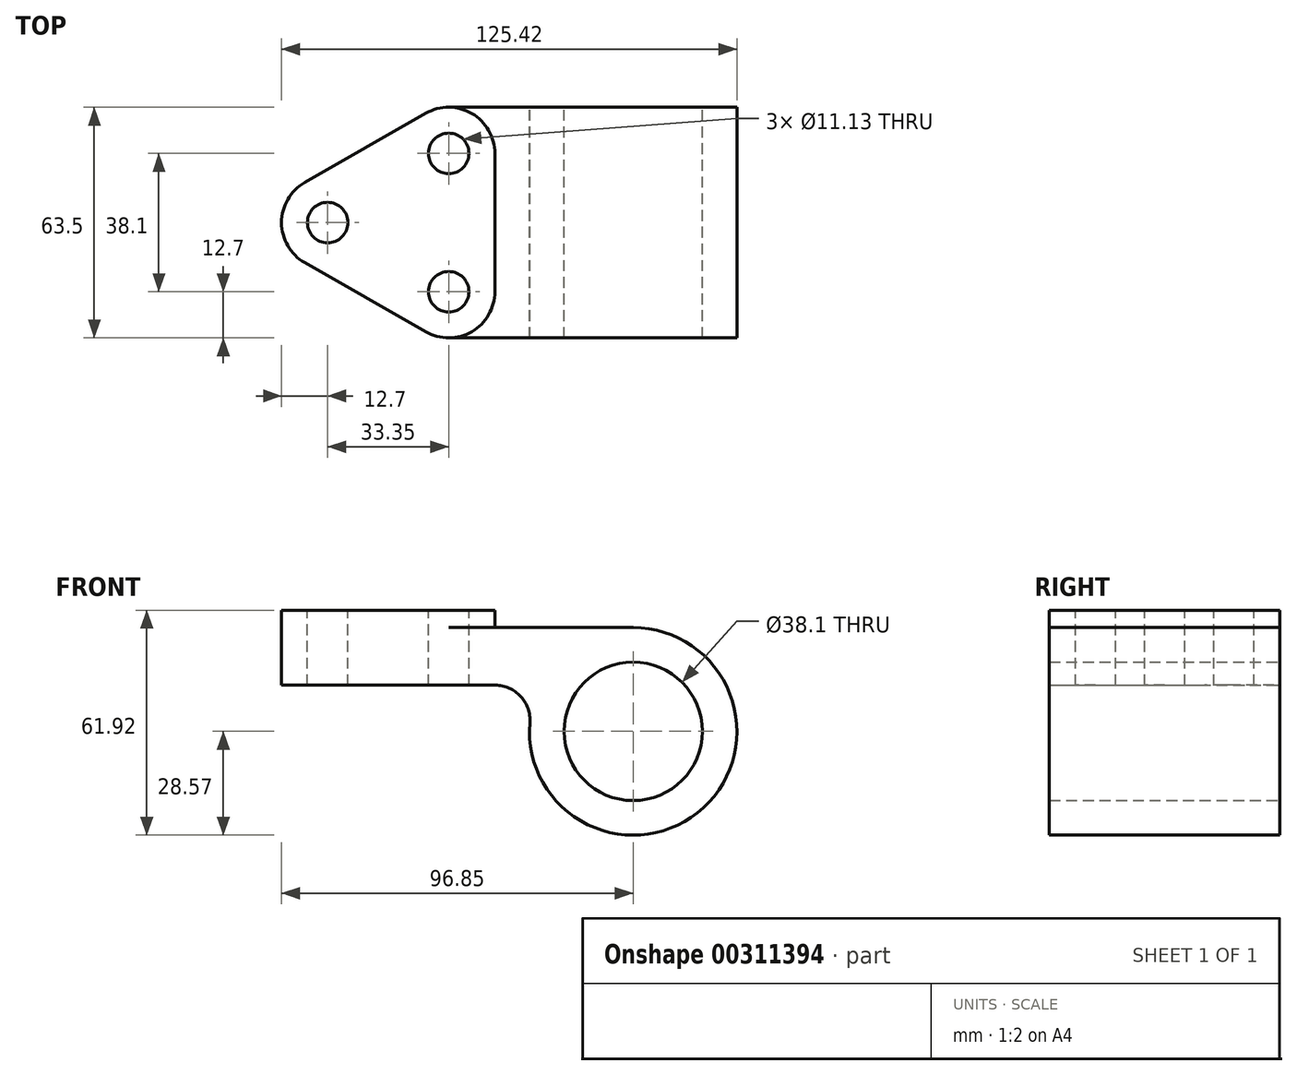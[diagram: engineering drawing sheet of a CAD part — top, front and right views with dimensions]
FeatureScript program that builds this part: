
annotation { "Feature Type Name" : "Feature", "Feature Type Description" : "" }
export const myFeature = defineFeature(function(context is Context, id is Id, definition is map)
    precondition{}
    {
        {
            var Q0;
            Q0=qCreatedBy(makeId("Front.planeOp"),FACE);
            var sketch = newSketch(context, id + "F0", { "sketchPlane" : qUnion([Q0])});
            skArc(sketch, "E0", {"start": v(-28.48, 2.38) * mm, "mid": v(19.35, -21.03) * mm, "end": v(0, 28.58) * mm});
            skCircle(sketch, "E1", {"center": v(0, 0) * mm, "radius": 19.05 * mm});
            skLineSegment(sketch, "E2", {"start": v(-37.97, 12.7) * mm, "end": v(-96.85, 12.7) * mm});
            skLineSegment(sketch, "E3", {"start": v(-96.85, 12.7) * mm, "end": v(-96.85, 28.57) * mm});
            skLineSegment(sketch, "E4", {"start": v(-38.1, 28.57) * mm, "end": v(0, 28.57) * mm});
            skLineSegment(sketch, "E5", {"start": v(-38.1, 28.57) * mm, "end": v(-38.1, 33.35) * mm});
            skLineSegment(sketch, "E6", {"start": v(-38.1, 33.35) * mm, "end": v(-96.85, 33.35) * mm});
            skLineSegment(sketch, "E7", {"start": v(-96.85, 33.35) * mm, "end": v(-96.85, 28.57) * mm});
            skPoint(sketch, "E8.visualSharp", {"position": v(-25.6, 12.7) * mm});
            skArc(sketch, "E8.filletArc", {"start": v(-28.48, 2.38) * mm, "mid": v(-30.96, 9.62) * mm, "end": v(-37.97, 12.7) * mm});
            skSolve(sketch);
        }
        {
            var Q0;
            Q0 = qSketchRegion(id + "F0", true);
            extrude(context, id + "F1", {"entities" : qUnion([Q0]), "depth" : 63.5 * mm});
        }
        {
            var Q0;
            Q0=makeQuery(id+"F1.opExtrude","SWEPT_FACE",FACE,{"disambiguationData":[OSD([sQuery(id+"F0.wireOp",EDGE,"E6")])]});
            var sketch = newSketch(context, id + "F2", { "sketchPlane" : qUnion([Q0])});
            skArc(sketch, "E9", {"start": v(-90.45, -20.72) * mm, "mid": v(-96.85, -31.75) * mm, "end": v(-90.45, -42.78) * mm});
            skPoint(sketch, "E9.centerSnap0", {"position": v(-38.1, -31.75) * mm});
            skArc(sketch, "E10", {"start": v(-38.1, -12.7) * mm, "mid": v(-44.42, -1.72) * mm, "end": v(-57.1, -1.67) * mm});
            skArc(sketch, "E11", {"start": v(-57.1, -61.83) * mm, "mid": v(-44.42, -61.78) * mm, "end": v(-38.1, -50.8) * mm});
            skLineSegment(sketch, "E12", {"start": v(-90.45, -20.72) * mm, "end": v(-57.1, -1.67) * mm});
            skLineSegment(sketch, "E13", {"start": v(-90.45, -42.78) * mm, "end": v(-57.1, -61.83) * mm});
            skLineSegment(sketch, "E14", {"start": v(-38.1, -12.7) * mm, "end": v(-38.1, -50.8) * mm});
            skCircle(sketch, "E15", {"center": v(-84.15, -31.75) * mm, "radius": 5.56 * mm});
            skCircle(sketch, "E16", {"center": v(-50.8, -12.7) * mm, "radius": 5.56 * mm});
            skCircle(sketch, "E17", {"center": v(-50.8, -50.8) * mm, "radius": 5.56 * mm});
            skSolve(sketch);
        }
        {
            var Q0;
            {var subQ6=sQuery(id+"F2.wireOp",EDGE,"E12");Q0=makeQuery(id+"F2.imprint","IMPRINT",FACE,{"disambiguationData":[TD([[makeQuery(id+"F2.imprint","IMPRINT",EDGE,{"derivedFrom":subQ6}),1.0]])]});}
            var Q1;
            {var subQ6=sQuery(id+"F2.wireOp",EDGE,"E13");Q1=makeQuery(id+"F2.imprint","IMPRINT",FACE,{"disambiguationData":[TD([[makeQuery(id+"F2.imprint","IMPRINT",EDGE,{"derivedFrom":subQ6}),-1.0]])]});}
            var Q2;
            {var subQ0=sQuery(id+"F2.wireOp",EDGE,"E11");var subQ1=sQuery(id+"F0.wireOp",EDGE,"E6");var subQ4=makeQuery(id+"F1.opExtrude","CAP_EDGE",EDGE,{"disambiguationData":[OSD([subQ1])],"isStart":false});var subQ5=makeQuery(id+"F2.imprint","INTERSECT",VERTEX,{"derivedFrom":[subQ4,subQ0]});Q2=makeQuery(id+"F2.imprint","IMPRINT",FACE,{"disambiguationData":[TD([[makeQuery(id+"F2.imprint","IMPRINT",EDGE,{"disambiguationData":[TD([[subQ5,1.0]])],"derivedFrom":subQ4}),-1.0]])]});}
            var Q3;
            {var subQ0=sQuery(id+"F2.wireOp",EDGE,"E10");var subQ1=sQuery(id+"F0.wireOp",EDGE,"E6");var subQ4=makeQuery(id+"F1.opExtrude","CAP_EDGE",EDGE,{"disambiguationData":[OSD([subQ1])],"isStart":true});var subQ5=makeQuery(id+"F2.imprint","INTERSECT",VERTEX,{"derivedFrom":[subQ4,subQ0]});Q3=makeQuery(id+"F2.imprint","IMPRINT",FACE,{"disambiguationData":[TD([[makeQuery(id+"F2.imprint","IMPRINT",EDGE,{"disambiguationData":[TD([[subQ5,1.0]])],"derivedFrom":subQ4}),1.0]])]});}
            extrude(context, id + "F3", {"entities" : qUnion([Q0, Q1, Q2, Q3]), "operationType" : NewBodyOperationType.REMOVE, "oppositeDirection" : true, "depth" : 4.78 * mm});
        }
        {
            var Q0;
            {var subQ6=sQuery(id+"F2.wireOp",EDGE,"E12");Q0=makeQuery(id+"F2.imprint","IMPRINT",FACE,{"disambiguationData":[TD([[makeQuery(id+"F2.imprint","IMPRINT",EDGE,{"derivedFrom":subQ6}),1.0]])]});}
            var Q1;
            {var subQ6=sQuery(id+"F2.wireOp",EDGE,"E13");Q1=makeQuery(id+"F2.imprint","IMPRINT",FACE,{"disambiguationData":[TD([[makeQuery(id+"F2.imprint","IMPRINT",EDGE,{"derivedFrom":subQ6}),-1.0]])]});}
            extrude(context, id + "F4", {"entities" : qUnion([Q0, Q1]), "operationType" : NewBodyOperationType.REMOVE, "oppositeDirection" : true, "depth" : 25.4 * mm});
        }
        {
            var Q0;
            Q0=makeQuery(id+"F2.imprint","IMPRINT",FACE,{"disambiguationData":[TD([[makeQuery(id+"F2.imprint","IMPRINT",EDGE,{"derivedFrom":sQuery(id+"F2.wireOp",EDGE,"E16")}),1.0]])]});
            var Q1;
            Q1=makeQuery(id+"F2.imprint","IMPRINT",FACE,{"disambiguationData":[TD([[makeQuery(id+"F2.imprint","IMPRINT",EDGE,{"derivedFrom":sQuery(id+"F2.wireOp",EDGE,"E15")}),1.0]])]});
            var Q2;
            Q2=makeQuery(id+"F2.imprint","IMPRINT",FACE,{"disambiguationData":[TD([[makeQuery(id+"F2.imprint","IMPRINT",EDGE,{"derivedFrom":sQuery(id+"F2.wireOp",EDGE,"E17")}),1.0]])]});
            extrude(context, id + "F5", {"entities" : qUnion([Q0, Q1, Q2]), "operationType" : NewBodyOperationType.REMOVE, "oppositeDirection" : true, "depth" : 25.4 * mm});
        }
    });
